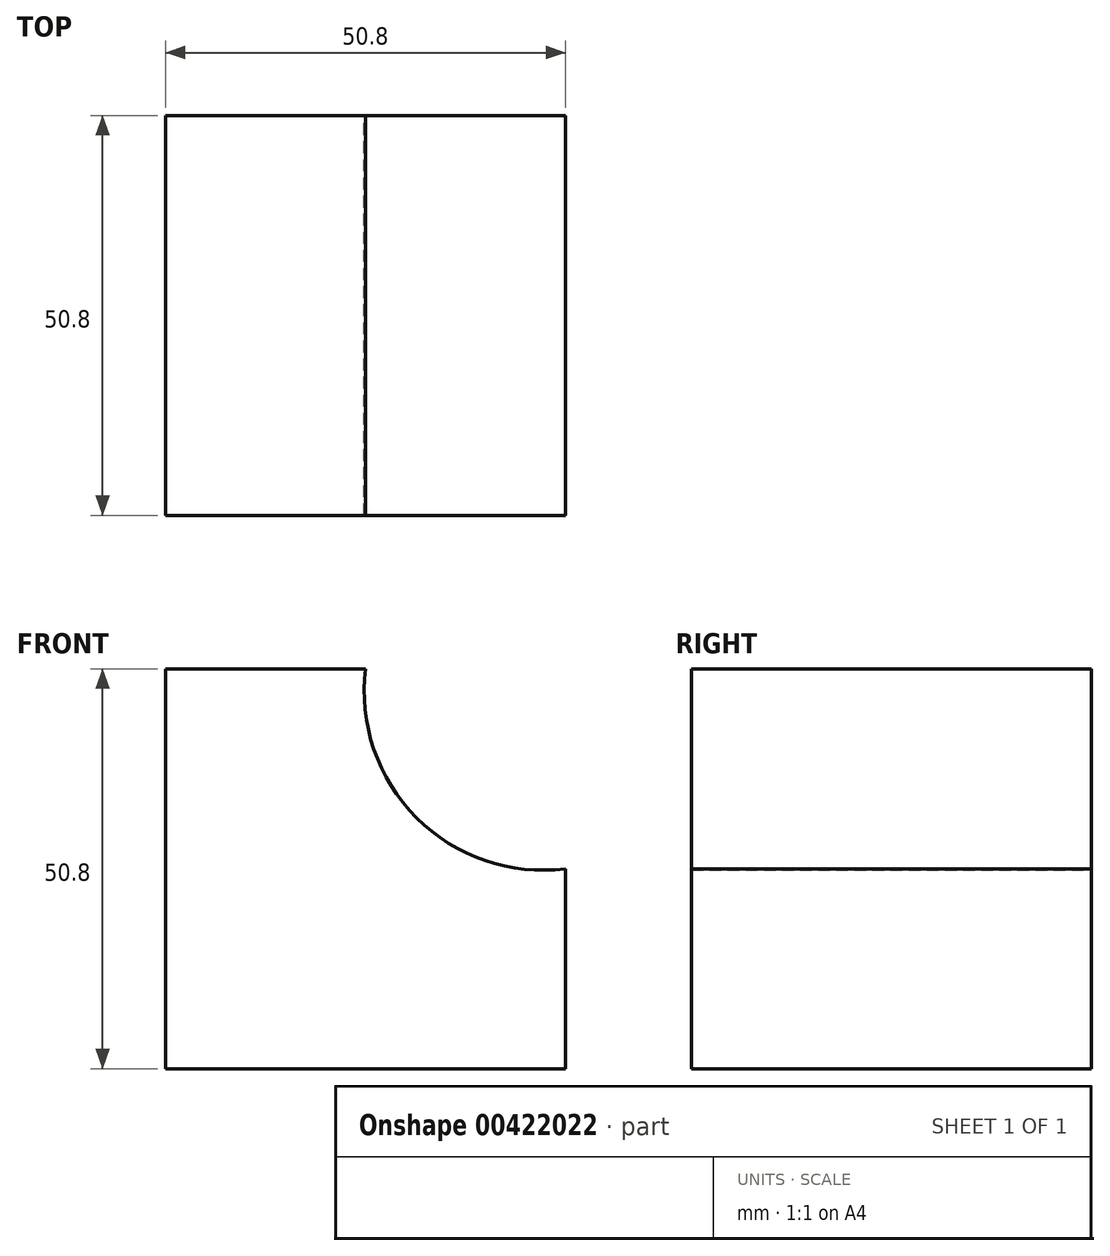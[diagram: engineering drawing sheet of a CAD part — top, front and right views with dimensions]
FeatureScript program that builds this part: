
annotation { "Feature Type Name" : "Feature", "Feature Type Description" : "" }
export const myFeature = defineFeature(function(context is Context, id is Id, definition is map)
    precondition{}
    {
        {
            var Q0;
            Q0=qCreatedBy(makeId("Front.planeOp"),FACE);
            var sketch = newSketch(context, id + "F0", { "sketchPlane" : qUnion([Q0])});
            skLineSegment(sketch, "E0", {"start": v(0, 0) * mm, "end": v(-50.8, 0) * mm});
            skLineSegment(sketch, "E1", {"start": v(-50.8, 0) * mm, "end": v(-50.8, 50.8) * mm});
            skLineSegment(sketch, "E2", {"start": v(-50.8, 50.8) * mm, "end": v(-25.4, 50.8) * mm});
            skLineSegment(sketch, "E3", {"start": v(0, 0) * mm, "end": v(0, 25.4) * mm});
            skArc(sketch, "E4", {"start": v(-25.4, 50.8) * mm, "mid": v(-18.93, 31.87) * mm, "end": v(0, 25.4) * mm});
            skSolve(sketch);
        }
        {
            var Q0;
            Q0 = qSketchRegion(id + "F0", true);
            extrude(context, id + "F1", {"entities" : qUnion([Q0]), "depth" : 50.8 * mm});
        }
    });
